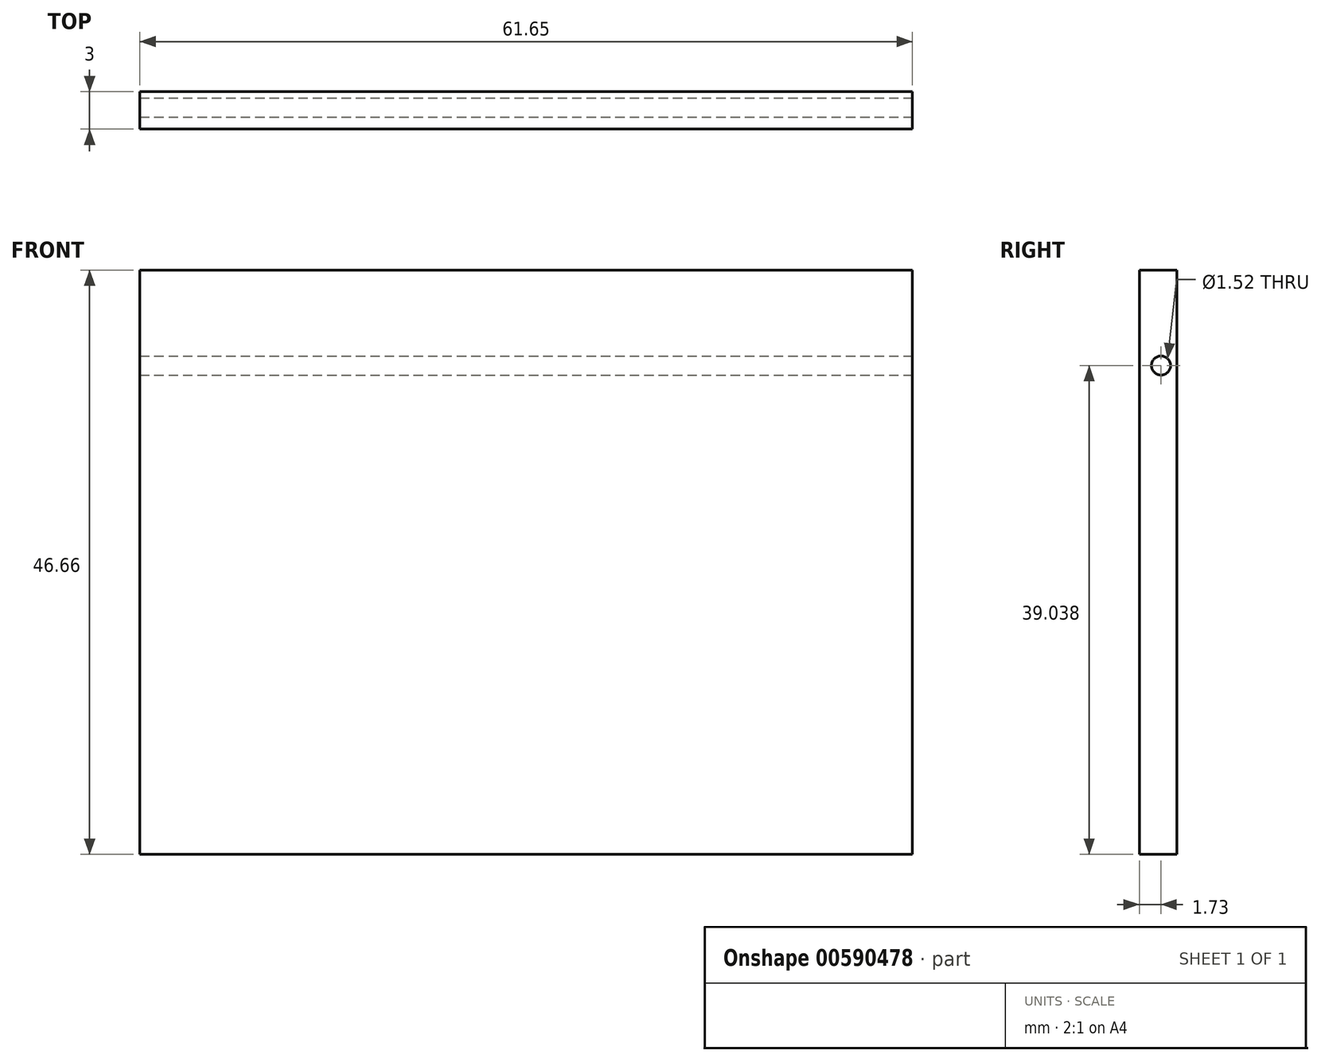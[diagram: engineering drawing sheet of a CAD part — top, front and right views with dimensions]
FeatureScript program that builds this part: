
annotation { "Feature Type Name" : "Feature", "Feature Type Description" : "" }
export const myFeature = defineFeature(function(context is Context, id is Id, definition is map)
    precondition{}
    {
        {
            var Q0;
            Q0=qCreatedBy(makeId("Front.planeOp"),FACE);
            var sketch = newSketch(context, id + "F0", { "sketchPlane" : qUnion([Q0])});
            skLineSegment(sketch, "E0.bottom", {"start": v(0, 0) * mm, "end": v(61.65, 0) * mm});
            skLineSegment(sketch, "E0.top", {"start": v(0, 46.66) * mm, "end": v(61.65, 46.66) * mm});
            skLineSegment(sketch, "E0.left", {"start": v(0, 0) * mm, "end": v(0, 46.66) * mm});
            skLineSegment(sketch, "E0.right", {"start": v(61.65, 0) * mm, "end": v(61.65, 46.66) * mm});
            skSolve(sketch);
        }
        {
            var Q0;
            Q0=makeQuery(id+"F0.imprint","IMPRINT",FACE,{"disambiguationData":[TD([[makeQuery(id+"F0.imprint","IMPRINT",EDGE,{"derivedFrom":sQuery(id+"F0.wireOp",EDGE,"E0.bottom")}),1.0]])]});
            extrude(context, id + "F1", {"entities" : qUnion([Q0]), "depth" : 3 * mm, "offsetDistance" : 25.4 * mm});
        }
        {
            var Q0;
            Q0=makeQuery(id+"F1.opExtrude","SWEPT_FACE",FACE,{"disambiguationData":[OSD([sQuery(id+"F0.wireOp",EDGE,"E0.right")])]});
            var sketch = newSketch(context, id + "F2", { "sketchPlane" : qUnion([Q0])});
            skCircle(sketch, "E1", {"center": v(-1.27, 39.04) * mm, "radius": 0.76 * mm});
            skSolve(sketch);
        }
        {
            var Q0;
            Q0 = qSketchRegion(id + "F2", true);
            extrude(context, id + "F3", {"entities" : qUnion([Q0]), "operationType" : NewBodyOperationType.REMOVE, "endBound" : BoundingType.THROUGH_ALL, "oppositeDirection" : true, "depth" : 25.4 * mm, "offsetDistance" : 25.4 * mm});
        }
    });
